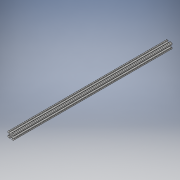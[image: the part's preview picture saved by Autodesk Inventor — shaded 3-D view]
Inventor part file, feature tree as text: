
AUTODESK INVENTOR PART (.ipt)
format: ipt  version: 2019 (Build 230136000, 136)  size: 237,056 bytes
history: native  units: in
note: dims shown in document units (in); Inventor stores cm internally (conversion verified against a paired STEP export)
features: extrude x1, sketch x1, other x1
ambient origin geometry x8: Origin, YZ Plane, XZ Plane, XY Plane, X Axis, Y Axis, Z Axis, Center Point
bodies: Solid1 (feature_tree)
feature tree (3):
  extrude  "Extrusion1"  [1 undecoded]
  sketch  "Sketch1"  dims[d0=27.0in d1=0.0in]
  other  "Boss-Extrude1"
note: 1 required parameter value undecoded (feature->parameter linkage not recoverable at this tier; creation-order binding heuristic only, values carry confidence <= 0.55)
